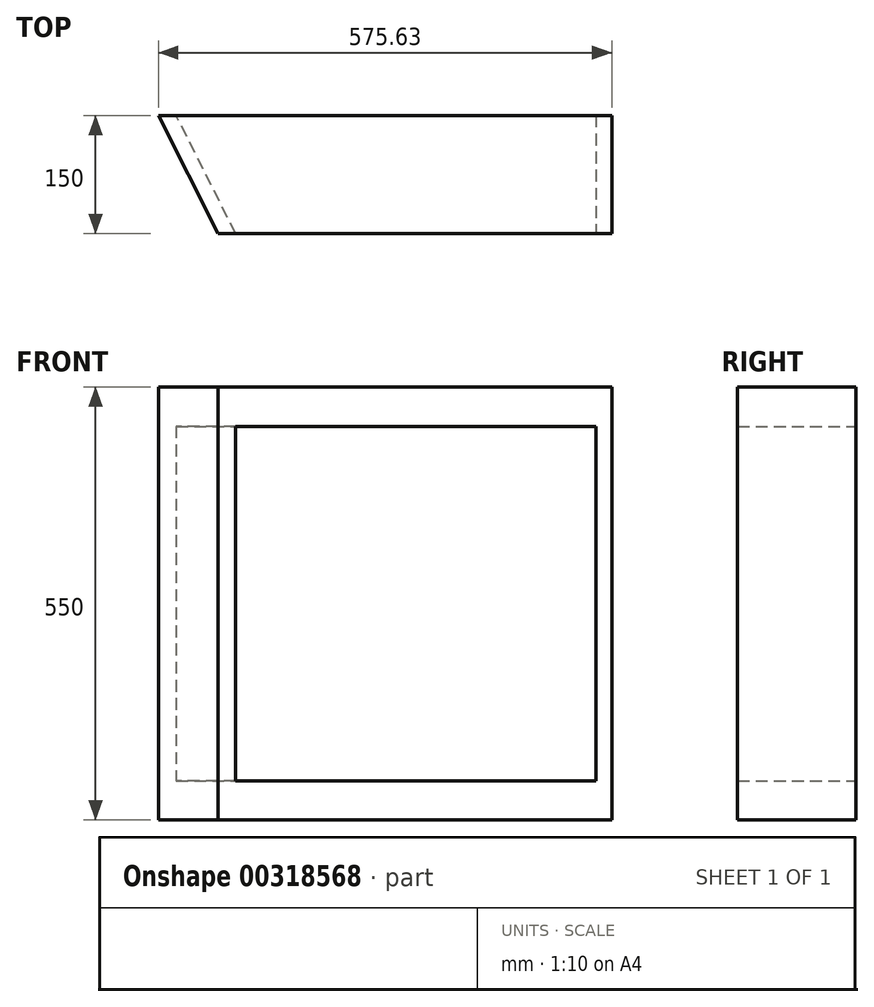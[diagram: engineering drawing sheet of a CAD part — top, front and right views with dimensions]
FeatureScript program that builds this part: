
annotation { "Feature Type Name" : "Feature", "Feature Type Description" : "" }
export const myFeature = defineFeature(function(context is Context, id is Id, definition is map)
    precondition{}
    {
        {
            var Q0;
            Q0=qCreatedBy(makeId("Top.planeOp"),FACE);
            var sketch = newSketch(context, id + "F0", { "sketchPlane" : qUnion([Q0])});
            skLineSegment(sketch, "E0.bottom", {"start": v(-326.22, 75.36) * mm, "end": v(249.4, 75.36) * mm});
            skLineSegment(sketch, "E0.top", {"start": v(-250.6, -74.64) * mm, "end": v(249.4, -74.64) * mm});
            skLineSegment(sketch, "E0.right", {"start": v(249.4, 75.36) * mm, "end": v(249.4, -74.64) * mm});
            skLineSegment(sketch, "E1", {"start": v(-250.6, -74.64) * mm, "end": v(-326.22, 75.36) * mm});
            skLineSegment(sketch, "E2.0", {"start": v(229.4, 75.36) * mm, "end": v(229.4, -74.64) * mm});
            skLineSegment(sketch, "E2.1", {"start": v(-250.6, 55.36) * mm, "end": v(229.4, 55.36) * mm});
            skLineSegment(sketch, "E2.2", {"start": v(-238.28, -54.64) * mm, "end": v(229.4, -54.64) * mm});
            skLineSegment(sketch, "E2.3", {"start": v(-228.2, -74.64) * mm, "end": v(-303.82, 75.36) * mm});
            skLineSegment(sketch, "E2.4", {"start": v(-293.74, 55.36) * mm, "end": v(-250.6, 55.36) * mm});
            skSolve(sketch);
        }
        {
            var Q0;
            Q0=makeQuery(id+"F0.imprint","IMPRINT",FACE,{"disambiguationData":[TD([[makeQuery(id+"F0.imprint","IMPRINT",EDGE,{"derivedFrom":sQuery(id+"F0.wireOp",EDGE,"E0.bottom")}),-1.0]])]});
            var Q1;
            Q1=makeQuery(id+"F0.imprint","IMPRINT",FACE,{"disambiguationData":[TD([[makeQuery(id+"F0.imprint","IMPRINT",EDGE,{"derivedFrom":sQuery(id+"F0.wireOp",EDGE,"E2.0")}),-1.0]])]});
            var Q2;
            {var subQ0=sQuery(id+"F0.wireOp",EDGE,"E1");Q2=makeQuery(id+"F0.imprint","IMPRINT",FACE,{"disambiguationData":[TD([[makeQuery(id+"F0.imprint","IMPRINT",EDGE,{"derivedFrom":subQ0}),-1.0]])]});}
            var Q3;
            {var subQ1=sQuery(id+"F0.wireOp",EDGE,"E2.1");Q3=makeQuery(id+"F0.imprint","IMPRINT",FACE,{"disambiguationData":[TD([[makeQuery(id+"F0.imprint","IMPRINT",EDGE,{"derivedFrom":subQ1}),-1.0]])]});}
            var Q4;
            {var subQ4=sQuery(id+"F0.wireOp",EDGE,"E0.right");Q4=makeQuery(id+"F0.imprint","IMPRINT",FACE,{"disambiguationData":[TD([[makeQuery(id+"F0.imprint","IMPRINT",EDGE,{"derivedFrom":subQ4}),-1.0]])]});}
            extrude(context, id + "F1", {"entities" : qUnion([Q0, Q1, Q2, Q3, Q4]), "depth" : 500 * mm, "hasSecondDirection" : true, "secondDirectionOppositeDirection" : true, "secondDirectionDepth" : 50 * mm});
        }
        {
            var Q0;
            {var subQ5=sQuery(id+"F0.wireOp",EDGE,"E2.2");Q0=makeQuery(id+"F0.imprint","IMPRINT",FACE,{"disambiguationData":[TD([[makeQuery(id+"F0.imprint","IMPRINT",EDGE,{"derivedFrom":subQ5}),-1.0]])]});}
            var Q1;
            {var subQ1=sQuery(id+"F0.wireOp",EDGE,"E2.1");Q1=makeQuery(id+"F0.imprint","IMPRINT",FACE,{"disambiguationData":[TD([[makeQuery(id+"F0.imprint","IMPRINT",EDGE,{"derivedFrom":subQ1}),-1.0]])]});}
            var Q2;
            {var subQ6=sQuery(id+"F0.wireOp",EDGE,"E2.1");Q2=makeQuery(id+"F0.imprint","IMPRINT",FACE,{"disambiguationData":[TD([[makeQuery(id+"F0.imprint","IMPRINT",EDGE,{"derivedFrom":subQ6}),1.0]])]});}
            extrude(context, id + "F2", {"entities" : qUnion([Q0, Q1, Q2]), "operationType" : NewBodyOperationType.REMOVE, "depth" : 450 * mm});
        }
        {
            var Q0;
            Q0=makeQuery(id+"F2.boolean.opBoolean","COPY",EDGE,{"derivedFrom":makeQuery(id+"F2.opExtrude","CAP_EDGE",EDGE,{"disambiguationData":[OSD([sQuery(id+"F0.wireOp",EDGE,"E2.3")])],"isStart":false})});
            cPoint(context, id + "F3", {"entities" : qUnion([Q0]), "parameter" : 0.5});
        }
        {
            var Q0;
            Q0=sQuery(id+"F0.wireOp",VERTEX,"E2.0.start");
            var Q1;
            Q1=sQuery(id+"F0.wireOp",VERTEX,"E2.0.end");
            var Q2;
            Q2 = qCreatedBy(id + "F3" ,VERTEX);
            cPlane(context, id + "F4", {"entities" : qUnion([Q0, Q1, Q2]), "cplaneType" : CPlaneType.THREE_POINT, "offset" : 25 * mm, "oppositeDirection" : true, "width" : 150 * mm, "height" : 150 * mm});
        }
        {
            var Q0;
            Q0=qCreatedBy(id+"F4.planeOp",FACE);
            var sketch = newSketch(context, id + "F5", { "sketchPlane" : qUnion([Q0])});
            skLineSegment(sketch, "E3.0", {"start": v(169.81, 75.36) * mm, "end": v(169.81, -74.64) * mm});
            skLineSegment(sketch, "E4.0", {"start": v(-471.48, -74.64) * mm, "end": v(169.81, -74.64) * mm});
            skLineSegment(sketch, "E5.0", {"start": v(-527.46, 75.36) * mm, "end": v(169.81, 75.36) * mm});
            skPoint(sketch, "E6.orphan", {"position": v(-168.91, -74.64) * mm});
            skPoint(sketch, "E7.orphan", {"position": v(-224.9, 75.36) * mm});
            skLineSegment(sketch, "E8.bottom", {"start": v(-690.8, -74.64) * mm, "end": v(319.17, -74.64) * mm});
            skLineSegment(sketch, "E8.top", {"start": v(-690.8, 75.36) * mm, "end": v(319.17, 75.36) * mm});
            skLineSegment(sketch, "E8.left", {"start": v(-690.8, -74.64) * mm, "end": v(-690.8, 75.36) * mm});
            skLineSegment(sketch, "E8.right", {"start": v(319.17, -74.64) * mm, "end": v(319.17, 75.36) * mm});
            skSolve(sketch);
        }
        {
            var Q0;
            {var subQ0=sQuery(id+"F5.wireOp",EDGE,"E3.0");Q0=makeQuery(id+"F5.imprint","IMPRINT",FACE,{"disambiguationData":[TD([[makeQuery(id+"F5.imprint","IMPRINT",EDGE,{"derivedFrom":subQ0}),-1.0]])]});}
            extrude(context, id + "F6", {"entities" : qUnion([Q0]), "endBound" : BoundingType.SYMMETRIC, "depth" : 50 * mm});
        }
        {
            var Q0;
            Q0=makeQuery(id+"F1.opExtrude","SWEPT_BODY",BODY,{"disambiguationData":[OSD([sQuery(id+"F0.wireOp",EDGE,"E0.bottom"),sQuery(id+"F0.wireOp",EDGE,"E0.top"),sQuery(id+"F0.wireOp",EDGE,"E0.right"),sQuery(id+"F0.wireOp",EDGE,"E1")])]});
            var Q1;
            Q1=makeQuery(id+"F6.opExtrude","SWEPT_BODY",BODY,{"disambiguationData":[OSD([sQuery(id+"F5.wireOp",EDGE,"E3.0"),sQuery(id+"F5.wireOp",EDGE,"E8.bottom"),sQuery(id+"F5.wireOp",EDGE,"E8.top"),sQuery(id+"F5.wireOp",EDGE,"E8.left")])]});
            booleanBodies(context, id + "F7", {"operationType" : BooleanOperationType.SUBTRACTION, "tools" : qUnion([Q0]), "targets" : qUnion([Q1]), "keepTools" : true});
        }
        {
            var Q0;
            Q0=makeQuery(id+"F7.opBoolean","SPLIT",BODY,{"disambiguationData":[OD(0.0)],"derivedFrom":makeQuery(id+"F6.opExtrude","SWEPT_BODY",BODY,{"disambiguationData":[OSD([sQuery(id+"F5.wireOp",EDGE,"E3.0"),sQuery(id+"F5.wireOp",EDGE,"E8.bottom"),sQuery(id+"F5.wireOp",EDGE,"E8.top"),sQuery(id+"F5.wireOp",EDGE,"E8.left")])]})});
            deleteBodies(context, id + "F8", {"entities" : qUnion([Q0])});
        }
    });
